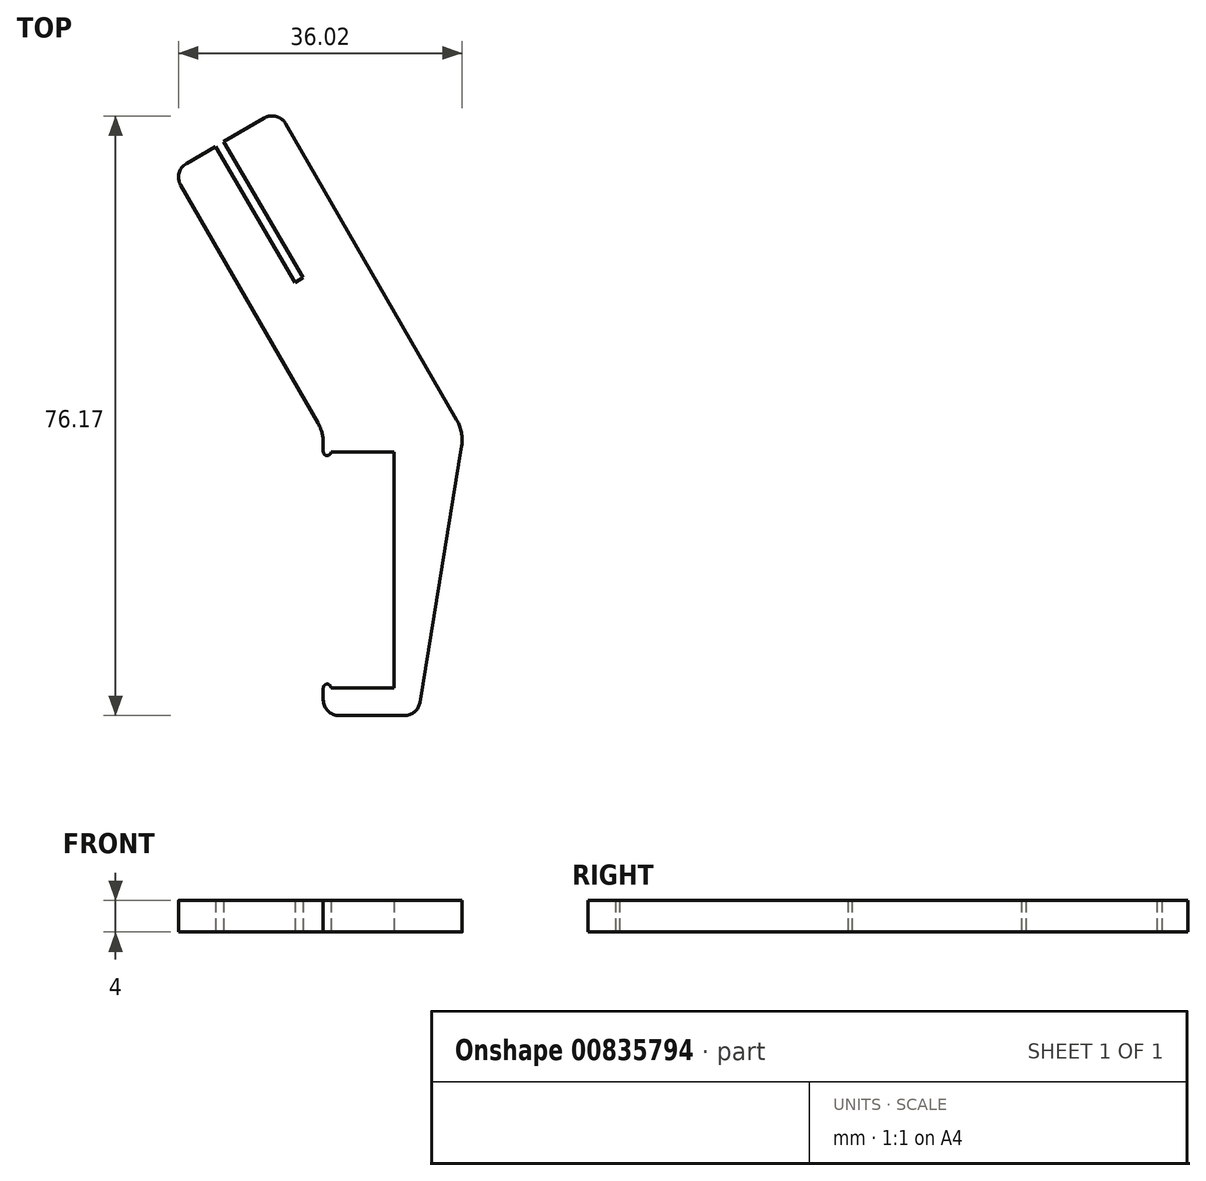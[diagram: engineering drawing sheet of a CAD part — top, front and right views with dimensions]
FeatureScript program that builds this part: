
annotation { "Feature Type Name" : "Feature", "Feature Type Description" : "" }
export const myFeature = defineFeature(function(context is Context, id is Id, definition is map)
    precondition{}
    {
        {
            var Q0;
            Q0=qCreatedBy(makeId("Top.planeOp"),FACE);
            var sketch = newSketch(context, id + "F0", { "sketchPlane" : qUnion([Q0])});
            skLineSegment(sketch, "E0", {"start": v(-11.69, 5.33) * mm, "end": v(-11.69, 2.83) * mm});
            skLineSegment(sketch, "E1", {"start": v(-11.69, -30.67) * mm, "end": v(0.31, -30.67) * mm});
            skLineSegment(sketch, "E2", {"start": v(6.16, 5.33) * mm, "end": v(0.31, -30.67) * mm});
            skLineSegment(sketch, "E3", {"start": v(-2.69, 2.83) * mm, "end": v(-2.69, -27.17) * mm});
            skLineSegment(sketch, "E4", {"start": v(-2.69, -27.17) * mm, "end": v(-10.71, -27.17) * mm});
            skLineSegment(sketch, "E5", {"start": v(-10.71, 2.83) * mm, "end": v(-10.71, -27.17) * mm, "construction": true});
            skArc(sketch, "E6", {"start": v(-10.71, 2.83) * mm, "mid": v(-11.2, 2.34) * mm, "end": v(-11.69, 2.83) * mm});
            skArc(sketch, "E7", {"start": v(-11.69, -27.17) * mm, "mid": v(-11.2, -26.68) * mm, "end": v(-10.71, -27.17) * mm});
            skPoint(sketch, "E8.start.orphan", {"position": v(-5.69, 5.33) * mm});
            skPoint(sketch, "E9.end.orphan", {"position": v(0.31, 5.33) * mm});
            skLineSegment(sketch, "E10.trimOffspring", {"start": v(-11.69, -27.17) * mm, "end": v(-11.69, -30.67) * mm});
            skLineSegment(sketch, "E11.trimOffspring", {"start": v(-10.71, 2.83) * mm, "end": v(-2.69, 2.83) * mm});
            skPoint(sketch, "E12.start.orphan", {"position": v(-11.69, 2.83) * mm});
            skPoint(sketch, "E13.start.orphan", {"position": v(10.16, 5.33) * mm});
            skPoint(sketch, "E14.end.orphan", {"position": v(9.96, 16.74) * mm});
            skPoint(sketch, "E14.start.orphan", {"position": v(9.96, 18.24) * mm});
            skPoint(sketch, "E15.center.orphan", {"position": v(10.06, 16.74) * mm});
            skPoint(sketch, "E16.trimOffspring.start.orphan", {"position": v(10.16, 16.74) * mm});
            skPoint(sketch, "E17.center.orphan", {"position": v(10.06, 18.24) * mm});
            skPoint(sketch, "E17.start.orphan", {"position": v(10.16, 18.24) * mm});
            skPoint(sketch, "E18.center.orphan", {"position": v(6.06, 18.24) * mm});
            skPoint(sketch, "E18.start.orphan", {"position": v(6.16, 18.24) * mm});
            skPoint(sketch, "E19.center.orphan", {"position": v(6.06, 16.74) * mm});
            skPoint(sketch, "E19.end.orphan", {"position": v(6.16, 16.74) * mm});
            skPoint(sketch, "E20.start.orphan", {"position": v(5.96, 18.24) * mm});
            skPoint(sketch, "E21.trimOffspring.end.orphan", {"position": v(5.96, 16.74) * mm});
            skPoint(sketch, "E22.orphan", {"position": v(-0.44, 18.24) * mm});
            skPoint(sketch, "E23.start.orphan", {"position": v(-0.44, 16.74) * mm});
            skPoint(sketch, "E24.trimOffspring.start.orphan", {"position": v(6.16, 11.03) * mm});
            skLineSegment(sketch, "E25", {"start": v(-11.69, 5.33) * mm, "end": v(-30.8, 38.44) * mm});
            skLineSegment(sketch, "E26", {"start": v(6.16, 5.33) * mm, "end": v(-17.46, 46.24) * mm});
            skLineSegment(sketch, "E27", {"start": v(-17.46, 46.24) * mm, "end": v(-24.36, 42.2) * mm});
            skLineSegment(sketch, "E28", {"start": v(-24.13, 42.34) * mm, "end": v(-10.16, 18.44) * mm, "construction": true});
            skLineSegment(sketch, "E29", {"start": v(-24.36, 42.2) * mm, "end": v(-14.27, 24.95) * mm});
            skLineSegment(sketch, "E30", {"start": v(-14.27, 24.95) * mm, "end": v(-15.3, 24.35) * mm});
            skLineSegment(sketch, "E31", {"start": v(-15.3, 24.35) * mm, "end": v(-25.4, 41.6) * mm});
            skLineSegment(sketch, "E32.trimOffspring", {"start": v(-25.4, 41.6) * mm, "end": v(-30.8, 38.44) * mm});
            skSolve(sketch);
        }
        {
            var Q0;
            Q0=makeQuery(id+"F0.imprint","IMPRINT",FACE,{"disambiguationData":[TD([[makeQuery(id+"F0.imprint","IMPRINT",EDGE,{"derivedFrom":sQuery(id+"F0.wireOp",EDGE,"E0")}),1.0]])]});
            extrude(context, id + "F1", {"entities" : qUnion([Q0]), "depth" : 4 * mm, "offsetDistance" : 25 * mm});
        }
        {
            var Q0;
            Q0=makeQuery(id+"F1.opExtrude","SWEPT_EDGE",EDGE,{"disambiguationData":[OSD([sQuery(id+"F0.wireOp",EDGE,"E1"),sQuery(id+"F0.wireOp",EDGE,"E2")])]});
            var Q1;
            Q1=makeQuery(id+"F1.opExtrude","SWEPT_EDGE",EDGE,{"disambiguationData":[OSD([sQuery(id+"F0.wireOp",EDGE,"E1"),sQuery(id+"F0.wireOp",EDGE,"E10.trimOffspring")])]});
            var Q2;
            Q2=makeQuery(id+"F1.opExtrude","SWEPT_EDGE",EDGE,{"disambiguationData":[OSD([sQuery(id+"F0.wireOp",EDGE,"E26"),sQuery(id+"F0.wireOp",EDGE,"E27")])]});
            var Q3;
            Q3=makeQuery(id+"F1.opExtrude","SWEPT_EDGE",EDGE,{"disambiguationData":[OSD([sQuery(id+"F0.wireOp",EDGE,"E25"),sQuery(id+"F0.wireOp",EDGE,"E32.trimOffspring")])]});
            fillet(context, id + "F2", {"entities" : qUnion([Q0, Q1, Q2, Q3]), "radius" : 2 * mm, "tangentPropagation" : true, "allowEdgeOverflow" : false});
        }
        {
            var Q0;
            Q0=makeQuery(id+"F1.opExtrude","SWEPT_EDGE",EDGE,{"disambiguationData":[OSD([sQuery(id+"F0.wireOp",EDGE,"E2"),sQuery(id+"F0.wireOp",EDGE,"E26")])]});
            var Q1;
            Q1=makeQuery(id+"F1.opExtrude","SWEPT_EDGE",EDGE,{"disambiguationData":[OSD([sQuery(id+"F0.wireOp",EDGE,"E0"),sQuery(id+"F0.wireOp",EDGE,"E25")])]});
            fillet(context, id + "F3", {"entities" : qUnion([Q0, Q1]), "radius" : 5 * mm, "tangentPropagation" : true, "allowEdgeOverflow" : false});
        }
    });
